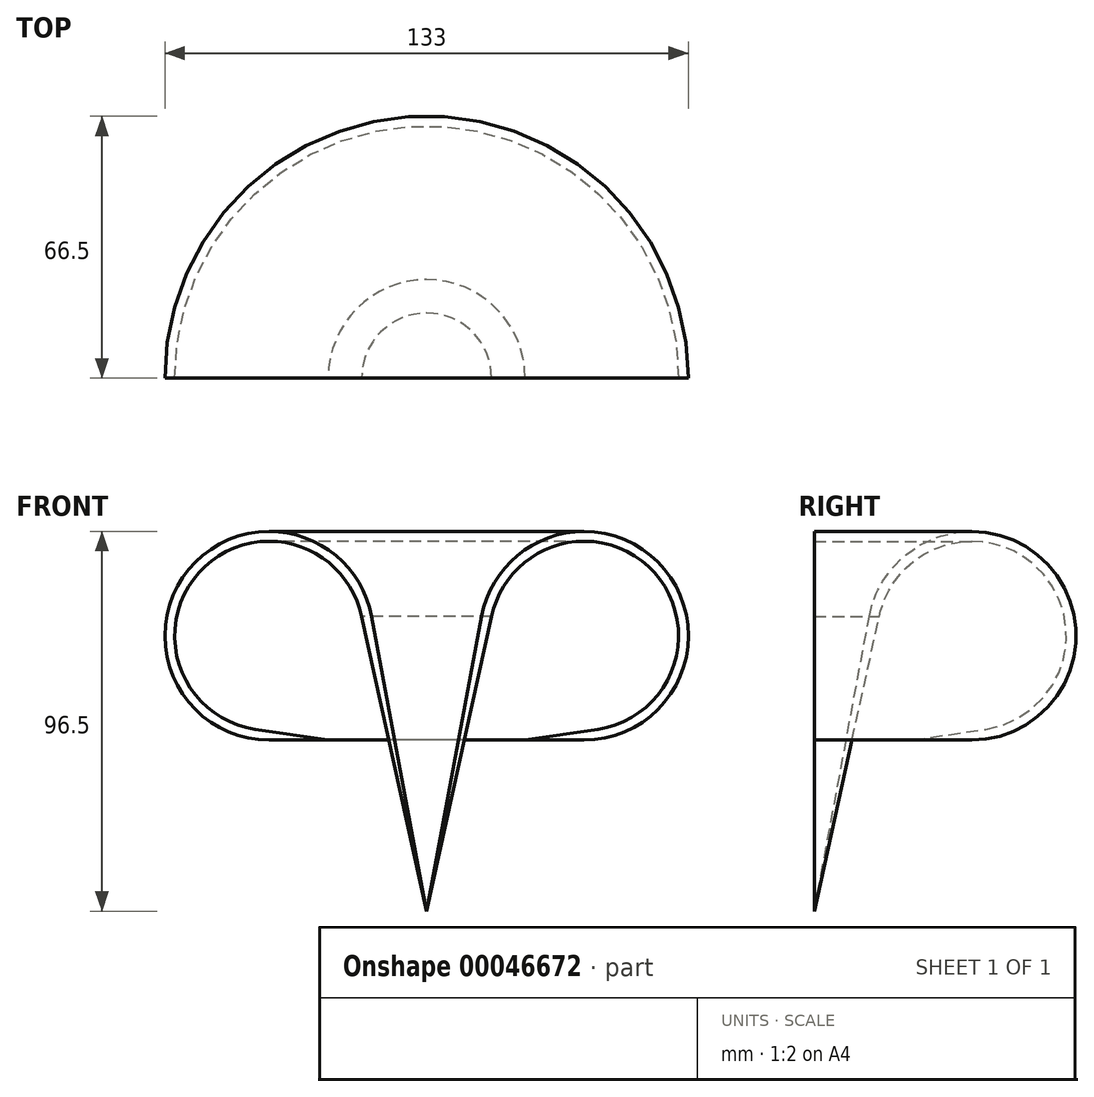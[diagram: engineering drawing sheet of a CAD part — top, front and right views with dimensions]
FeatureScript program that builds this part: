
annotation { "Feature Type Name" : "Feature", "Feature Type Description" : "" }
export const myFeature = defineFeature(function(context is Context, id is Id, definition is map)
    precondition{}
    {
        {
            var Q0;
            Q0=qCreatedBy(makeId("Front.planeOp"),FACE);
            var sketch = newSketch(context, id + "F0", { "sketchPlane" : qUnion([Q0])});
            skArc(sketch, "E0", {"start": v(-13.95, 74.85) * mm, "mid": v(-60.38, 86.94) * mm, "end": v(-40, 43.5) * mm});
            skLineSegment(sketch, "E1", {"start": v(0, 0) * mm, "end": v(-13.95, 74.85) * mm});
            skLineSegment(sketch, "E2", {"start": v(-25, 43.5) * mm, "end": v(-40, 43.5) * mm});
            skLineSegment(sketch, "E3", {"start": v(0, 0) * mm, "end": v(-16.5, 74.85) * mm});
            skLineSegment(sketch, "E4", {"start": v(-25, 43.5) * mm, "end": v(-43.54, 46.26) * mm});
            skArc(sketch, "E5", {"start": v(-16.5, 74.85) * mm, "mid": v(-57.44, 86.5) * mm, "end": v(-43.54, 46.26) * mm});
            skLineSegment(sketch, "E6", {"start": v(0, 0) * mm, "end": v(0, -19.02) * mm});
            skSolve(sketch);
        }
        {
            var Q0;
            Q0 = qSketchRegion(id + "F0", true);
            var Q1;
            Q1=sQuery(id+"F0.wireOp",EDGE,"E6");
            revolve(context, id + "F1", {"entities" : qUnion([Q0]), "axis" : qUnion([Q1]), "revolveType" : RevolveType.ONE_DIRECTION, "angle" : 180 * degree});
        }
    });
